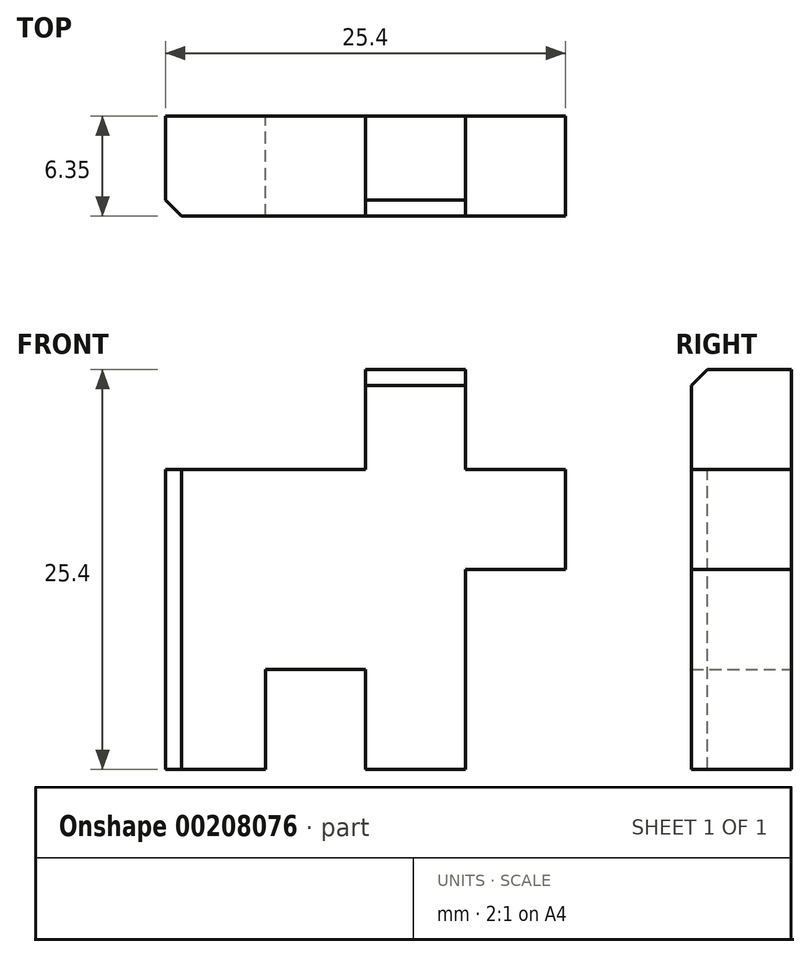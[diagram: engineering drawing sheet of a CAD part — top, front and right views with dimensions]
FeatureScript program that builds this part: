
annotation { "Feature Type Name" : "Feature", "Feature Type Description" : "" }
export const myFeature = defineFeature(function(context is Context, id is Id, definition is map)
    precondition{}
    {
        {
            var Q0;
            Q0=qCreatedBy(makeId("Front.planeOp"),FACE);
            var sketch = newSketch(context, id + "F0", { "sketchPlane" : qUnion([Q0])});
            skLineSegment(sketch, "E0.bottom", {"start": v(6.35, -12.7) * mm, "end": v(0, -12.7) * mm});
            skLineSegment(sketch, "E0.top", {"start": v(6.35, 12.7) * mm, "end": v(0, 12.7) * mm});
            skLineSegment(sketch, "E0.left", {"start": v(12.7, 0) * mm, "end": v(12.7, 6.35) * mm});
            skLineSegment(sketch, "E0.right", {"start": v(-12.7, -12.7) * mm, "end": v(-12.7, 6.35) * mm});
            skPoint(sketch, "E0.middle", {"position": v(0, 0) * mm});
            skLineSegment(sketch, "E1", {"start": v(0, 12.7) * mm, "end": v(0, 6.35) * mm});
            skLineSegment(sketch, "E2", {"start": v(0, 6.35) * mm, "end": v(-12.7, 6.35) * mm});
            skPoint(sketch, "E3.orphan", {"position": v(-17.1, 6.35) * mm});
            skLineSegment(sketch, "E4", {"start": v(0, 6.35) * mm, "end": v(12.7, 6.35) * mm});
            skLineSegment(sketch, "E5", {"start": v(6.35, 6.35) * mm, "end": v(6.35, 12.7) * mm});
            skPoint(sketch, "E6.orphan", {"position": v(12.7, 12.7) * mm});
            skPoint(sketch, "E7.orphan", {"position": v(-12.7, 12.7) * mm});
            skLineSegment(sketch, "E8", {"start": v(6.35, 0) * mm, "end": v(6.35, -15.08) * mm});
            skLineSegment(sketch, "E9", {"start": v(6.35, 0) * mm, "end": v(12.7, 0) * mm});
            skPoint(sketch, "E10.orphan", {"position": v(12.7, -12.7) * mm});
            skLineSegment(sketch, "E11", {"start": v(0, -12.7) * mm, "end": v(0, -6.35) * mm});
            skLineSegment(sketch, "E12", {"start": v(-6.35, -12.7) * mm, "end": v(-6.35, -6.35) * mm});
            skLineSegment(sketch, "E13", {"start": v(0, -6.35) * mm, "end": v(-6.35, -6.35) * mm});
            skLineSegment(sketch, "E14.trimOffspring", {"start": v(-6.35, -12.7) * mm, "end": v(-12.7, -12.7) * mm});
            skPoint(sketch, "E15.orphan", {"position": v(-10.81, -6.35) * mm});
            skSolve(sketch);
        }
        {
            var Q0;
            Q0 = qSketchRegion(id + "F0", true);
            extrude(context, id + "F1", {"entities" : qUnion([Q0]), "depth" : 6.35 * mm});
        }
        {
            var Q0;
            Q0=makeQuery(id+"F1.opExtrude","CAP_EDGE",EDGE,{"disambiguationData":[OSD([sQuery(id+"F0.wireOp",EDGE,"E0.right")])],"isStart":false});
            chamfer(context, id + "F2", {"entities" : qUnion([Q0]), "width" : 1.02 * mm, "tangentPropagation" : true});
        }
        {
            var Q0;
            Q0=makeQuery(id+"F1.opExtrude","CAP_EDGE",EDGE,{"disambiguationData":[OSD([sQuery(id+"F0.wireOp",EDGE,"E0.top")])],"isStart":false});
            chamfer(context, id + "F3", {"entities" : qUnion([Q0]), "width" : 1.02 * mm, "tangentPropagation" : true});
        }
    });
